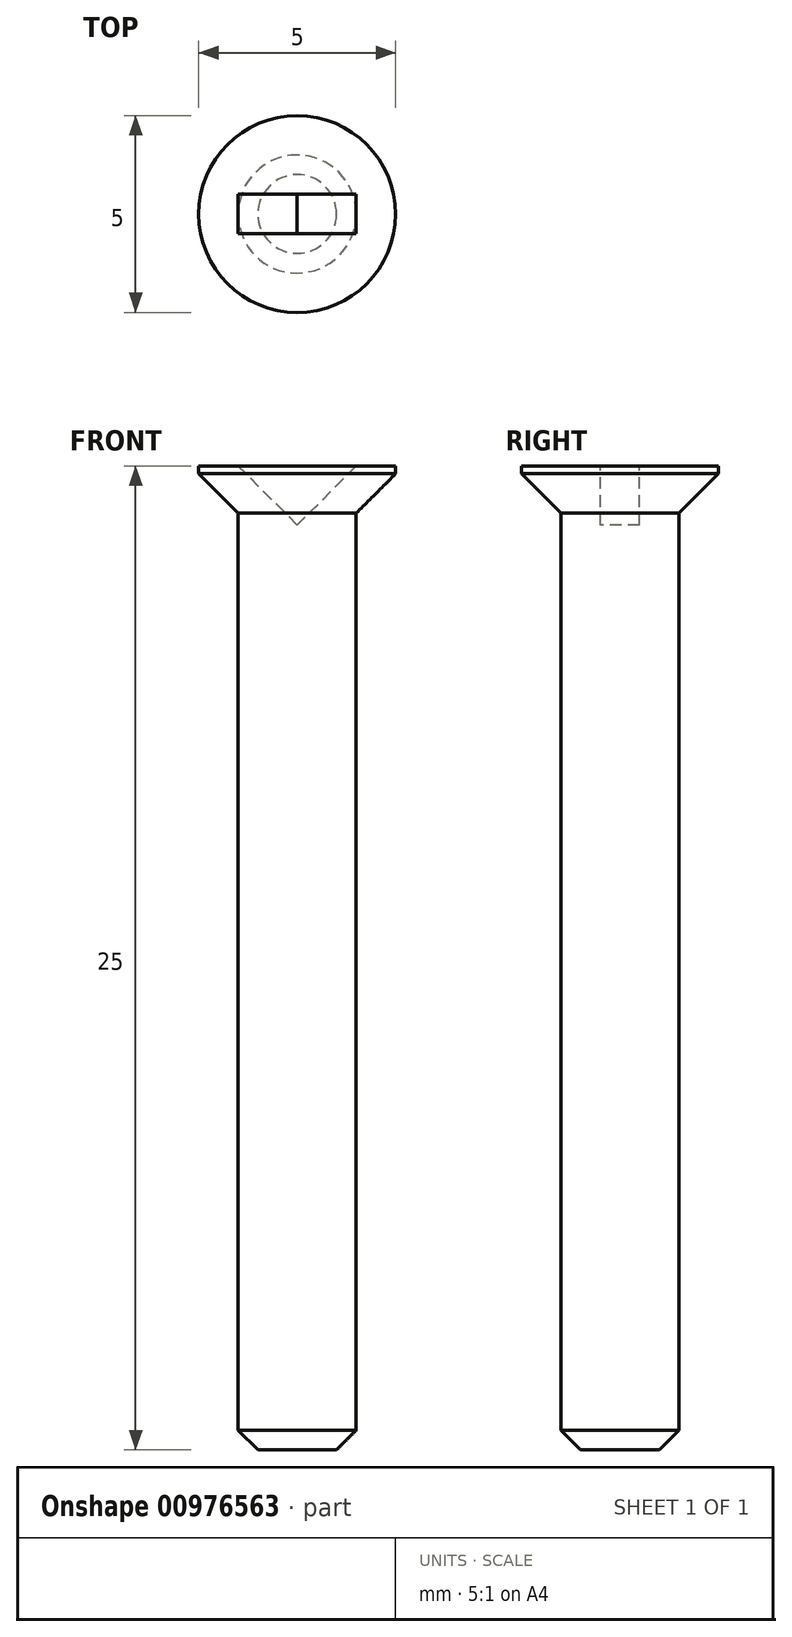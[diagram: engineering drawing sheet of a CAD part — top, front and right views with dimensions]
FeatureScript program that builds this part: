
annotation { "Feature Type Name" : "Feature", "Feature Type Description" : "" }
export const myFeature = defineFeature(function(context is Context, id is Id, definition is map)
    precondition{}
    {
        {
            var Q0;
            Q0=qCreatedBy(makeId("Front.planeOp"),FACE);
            var sketch = newSketch(context, id + "F0", { "sketchPlane" : qUnion([Q0])});
            skLineSegment(sketch, "E0", {"start": v(0, 0) * mm, "end": v(0, -25) * mm});
            skLineSegment(sketch, "E1", {"start": v(0, -25) * mm, "end": v(-1.5, -25) * mm});
            skLineSegment(sketch, "E2", {"start": v(-1.5, -25) * mm, "end": v(-1.5, -1.2) * mm});
            skLineSegment(sketch, "E3", {"start": v(-1.5, -1.2) * mm, "end": v(-2.5, -0.2) * mm});
            skLineSegment(sketch, "E4", {"start": v(-2.5, -0.2) * mm, "end": v(-2.5, 0) * mm});
            skLineSegment(sketch, "E5", {"start": v(-2.5, 0) * mm, "end": v(0, 0) * mm});
            skSolve(sketch);
        }
        {
            var Q0;
            Q0=makeQuery(id+"F0.imprint","IMPRINT",FACE,{"disambiguationData":[TD([[makeQuery(id+"F0.imprint","IMPRINT",EDGE,{"derivedFrom":sQuery(id+"F0.wireOp",EDGE,"E0")}),-1.0]])]});
            var Q1;
            Q1=sQuery(id+"F0.wireOp",EDGE,"E0");
            revolve(context, id + "F1", {"surfaceOperationType" : NewSurfaceOperationType.NEW, "entities" : qUnion([Q0]), "axis" : qUnion([Q1]), "revolveType" : RevolveType.FULL});
        }
        {
            var Q0;
            Q0=makeQuery(id+"F1.opRevolve","SWEPT_EDGE",EDGE,{"disambiguationData":[OSD([sQuery(id+"F0.wireOp",EDGE,"E1"),sQuery(id+"F0.wireOp",EDGE,"E2")])]});
            chamfer(context, id + "F2", {"entities" : qUnion([Q0]), "width" : .5 * mm, "tangentPropagation" : true});
        }
        {
            var Q0;
            Q0=qCreatedBy(makeId("Front.planeOp"),FACE);
            var sketch = newSketch(context, id + "F3", { "sketchPlane" : qUnion([Q0])});
            skLineSegment(sketch, "E6", {"start": v(-1.5, 0) * mm, "end": v(1.5, 0) * mm});
            skLineSegment(sketch, "E7", {"start": v(1.5, 0) * mm, "end": v(0, -1.5) * mm});
            skLineSegment(sketch, "E8", {"start": v(0, -1.5) * mm, "end": v(-1.5, 0) * mm});
            skSolve(sketch);
        }
        {
            var Q0;
            Q0=qSketchRegion(id+"F3",true);
            extrude(context, id + "F4", {"entities" : qUnion([Q0]), "operationType" : NewBodyOperationType.REMOVE, "endBound" : BoundingType.SYMMETRIC, "oppositeDirection" : true, "depth" : 1 * mm, "offsetDistance" : 25 * mm});
        }
    });
